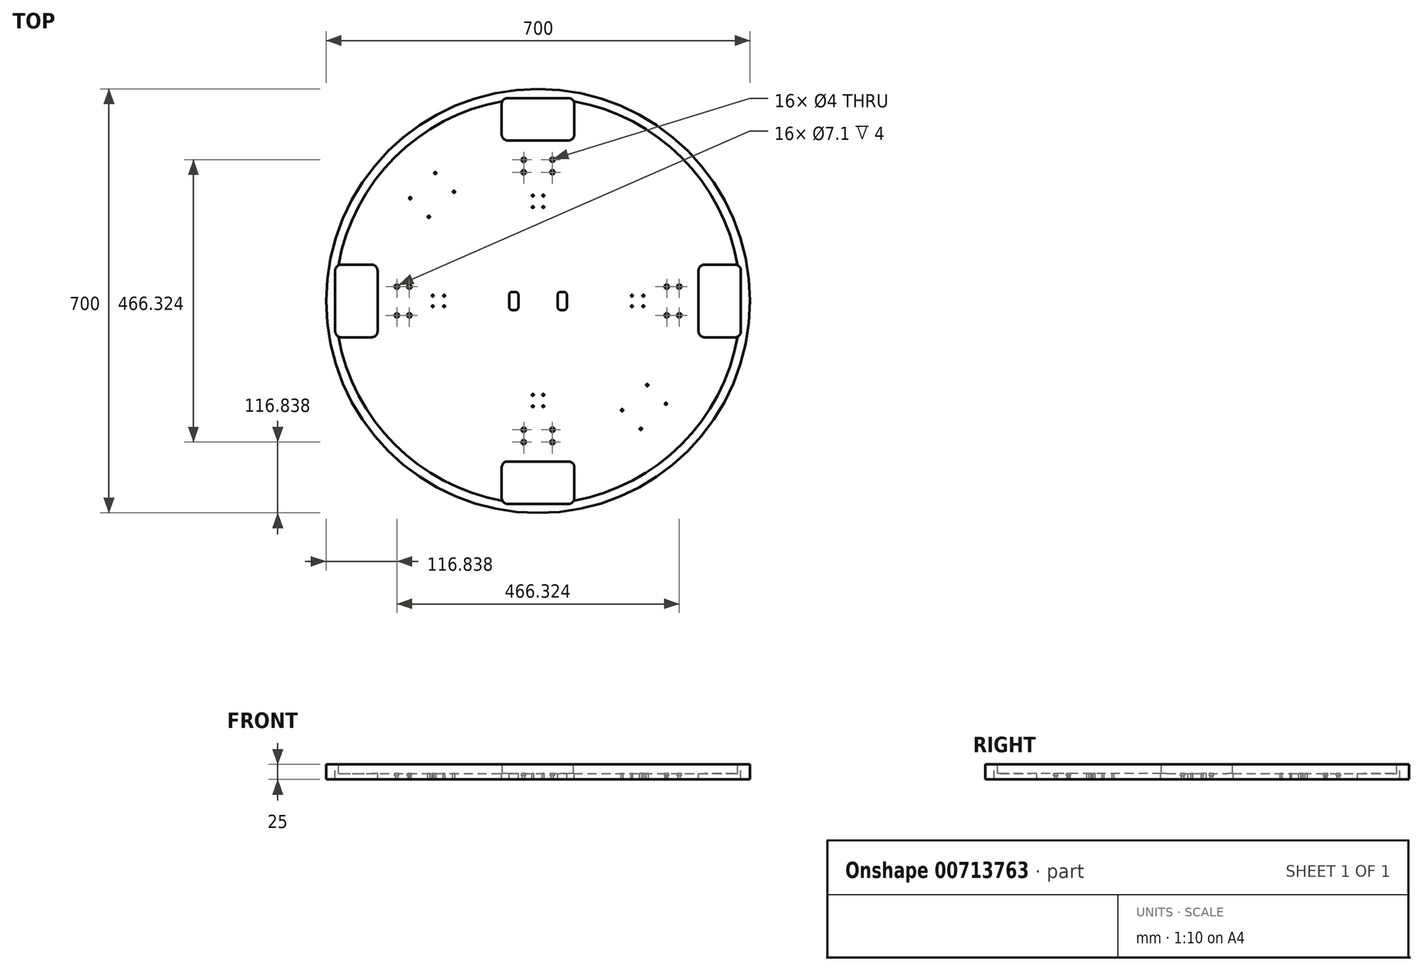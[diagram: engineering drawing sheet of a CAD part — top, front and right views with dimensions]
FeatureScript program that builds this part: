
annotation { "Feature Type Name" : "Feature", "Feature Type Description" : "" }
export const myFeature = defineFeature(function(context is Context, id is Id, definition is map)
    precondition{}
    {
        {
            var Q0;
            Q0=qCreatedBy(makeId("Top.planeOp"),FACE);
            var sketch = newSketch(context, id + "F0", { "sketchPlane" : qUnion([Q0])});
            skCircle(sketch, "E0", {"center": v(0, 0) * mm, "radius": 350 * mm});
            skSolve(sketch);
        }
        {
            var Q0;
            Q0 = qSketchRegion(id + "F0", true);
            extrude(context, id + "F1", {"entities" : qUnion([Q0]), "depth" : 25 * mm, "offsetDistance" : 25 * mm});
        }
        {
            var Q0;
            Q0=makeQuery(id+"F1.opExtrude","CAP_FACE",FACE,{"disambiguationData":[OSD([sQuery(id+"F0.wireOp",EDGE,"E0")])],"isStart":false});
            var sketch = newSketch(context, id + "F2", { "sketchPlane" : qUnion([Q0])});
            skLineSegment(sketch, "E1", {"start": v(0, 350) * mm, "end": v(0, -350) * mm});
            skLineSegment(sketch, "E2", {"start": v(-350, 0) * mm, "end": v(350, 0) * mm});
            skLineSegment(sketch, "E3.bottom", {"start": v(50, 265) * mm, "end": v(-50, 265) * mm});
            skLineSegment(sketch, "E3.top", {"start": v(50, 335) * mm, "end": v(-50, 335) * mm});
            skLineSegment(sketch, "E3.left", {"start": v(60, 275) * mm, "end": v(60, 325) * mm});
            skLineSegment(sketch, "E3.right", {"start": v(-60, 275) * mm, "end": v(-60, 325) * mm});
            skPoint(sketch, "E3.middle", {"position": v(0, 300) * mm});
            skPoint(sketch, "E4.visualSharp", {"position": v(-60, 335) * mm});
            skArc(sketch, "E4.filletArc", {"start": v(-50, 335) * mm, "mid": v(-57.07, 332.07) * mm, "end": v(-60, 325) * mm});
            skPoint(sketch, "E5.visualSharp", {"position": v(-60, 265) * mm});
            skArc(sketch, "E5.filletArc", {"start": v(-60, 275) * mm, "mid": v(-57.07, 267.93) * mm, "end": v(-50, 265) * mm});
            skPoint(sketch, "E6.visualSharp", {"position": v(60, 265) * mm});
            skArc(sketch, "E6.filletArc", {"start": v(50, 265) * mm, "mid": v(57.07, 267.93) * mm, "end": v(60, 275) * mm});
            skPoint(sketch, "E7.visualSharp", {"position": v(60, 335) * mm});
            skArc(sketch, "E7.filletArc", {"start": v(60, 325) * mm, "mid": v(57.07, 332.07) * mm, "end": v(50, 335) * mm});
            skLineSegment(sketch, "E8.bottom", {"start": v(-275, 60) * mm, "end": v(-325, 60) * mm});
            skLineSegment(sketch, "E8.top", {"start": v(-275, -60) * mm, "end": v(-325, -60) * mm});
            skLineSegment(sketch, "E8.left", {"start": v(-265, 50) * mm, "end": v(-265, -50) * mm});
            skLineSegment(sketch, "E8.right", {"start": v(-335, 50) * mm, "end": v(-335, -50) * mm});
            skPoint(sketch, "E8.middle", {"position": v(-300, 0) * mm});
            skPoint(sketch, "E9.visualSharp", {"position": v(-335, 60) * mm});
            skArc(sketch, "E9.filletArc", {"start": v(-325, 60) * mm, "mid": v(-332.07, 57.07) * mm, "end": v(-335, 50) * mm});
            skPoint(sketch, "E10.visualSharp", {"position": v(-265, 60) * mm});
            skArc(sketch, "E10.filletArc", {"start": v(-265, 50) * mm, "mid": v(-267.93, 57.07) * mm, "end": v(-275, 60) * mm});
            skPoint(sketch, "E11.visualSharp", {"position": v(-265, -60) * mm});
            skArc(sketch, "E11.filletArc", {"start": v(-275, -60) * mm, "mid": v(-267.93, -57.07) * mm, "end": v(-265, -50) * mm});
            skPoint(sketch, "E12.visualSharp", {"position": v(-335, -60) * mm});
            skArc(sketch, "E12.filletArc", {"start": v(-335, -50) * mm, "mid": v(-332.07, -57.07) * mm, "end": v(-325, -60) * mm});
            skLineSegment(sketch, "E13.bottom", {"start": v(50, -265) * mm, "end": v(-50, -265) * mm});
            skLineSegment(sketch, "E13.top", {"start": v(50, -335) * mm, "end": v(-50, -335) * mm});
            skLineSegment(sketch, "E13.left", {"start": v(60, -275) * mm, "end": v(60, -325) * mm});
            skLineSegment(sketch, "E13.right", {"start": v(-60, -275) * mm, "end": v(-60, -325) * mm});
            skPoint(sketch, "E13.middle", {"position": v(0, -300) * mm});
            skLineSegment(sketch, "E14.bottom", {"start": v(275, 60) * mm, "end": v(325, 60) * mm});
            skLineSegment(sketch, "E14.top", {"start": v(275, -60) * mm, "end": v(325, -60) * mm});
            skLineSegment(sketch, "E14.left", {"start": v(265, 50) * mm, "end": v(265, -50) * mm});
            skLineSegment(sketch, "E14.right", {"start": v(335, 50) * mm, "end": v(335, -50) * mm});
            skPoint(sketch, "E14.middle", {"position": v(300, 0) * mm});
            skPoint(sketch, "E15.visualSharp", {"position": v(265, 60) * mm});
            skArc(sketch, "E15.filletArc", {"start": v(275, 60) * mm, "mid": v(267.93, 57.07) * mm, "end": v(265, 50) * mm});
            skPoint(sketch, "E16.visualSharp", {"position": v(335, 60) * mm});
            skArc(sketch, "E16.filletArc", {"start": v(335, 50) * mm, "mid": v(332.07, 57.07) * mm, "end": v(325, 60) * mm});
            skPoint(sketch, "E17.visualSharp", {"position": v(335, -60) * mm});
            skArc(sketch, "E17.filletArc", {"start": v(325, -60) * mm, "mid": v(332.07, -57.07) * mm, "end": v(335, -50) * mm});
            skPoint(sketch, "E18.visualSharp", {"position": v(265, -60) * mm});
            skArc(sketch, "E18.filletArc", {"start": v(265, -50) * mm, "mid": v(267.93, -57.07) * mm, "end": v(275, -60) * mm});
            skPoint(sketch, "E19.visualSharp", {"position": v(60, -265) * mm});
            skArc(sketch, "E19.filletArc", {"start": v(60, -275) * mm, "mid": v(57.07, -267.93) * mm, "end": v(50, -265) * mm});
            skPoint(sketch, "E20.visualSharp", {"position": v(60, -335) * mm});
            skArc(sketch, "E20.filletArc", {"start": v(50, -335) * mm, "mid": v(57.07, -332.07) * mm, "end": v(60, -325) * mm});
            skPoint(sketch, "E21.visualSharp", {"position": v(-60, -335) * mm});
            skArc(sketch, "E21.filletArc", {"start": v(-60, -325) * mm, "mid": v(-57.07, -332.07) * mm, "end": v(-50, -335) * mm});
            skPoint(sketch, "E22.visualSharp", {"position": v(-60, -265) * mm});
            skArc(sketch, "E22.filletArc", {"start": v(-50, -265) * mm, "mid": v(-57.07, -267.93) * mm, "end": v(-60, -275) * mm});
            skSolve(sketch);
        }
        {
            var Q0;
            Q0 = qSketchRegion(id + "F2", true);
            extrude(context, id + "F3", {"entities" : qUnion([Q0]), "operationType" : NewBodyOperationType.REMOVE, "oppositeDirection" : true, "depth" : 25 * mm, "offsetDistance" : 25 * mm});
        }
        {
            var Q0;
            Q0=makeQuery(id+"F1.opExtrude","CAP_FACE",FACE,{"disambiguationData":[OSD([sQuery(id+"F0.wireOp",EDGE,"E0")])],"isStart":false});
            var sketch = newSketch(context, id + "F4", { "sketchPlane" : qUnion([Q0])});
            skCircle(sketch, "E23", {"center": v(0, 0) * mm, "radius": 335 * mm});
            skSolve(sketch);
        }
        {
            var Q0;
            Q0 = qSketchRegion(id + "F4", true);
            extrude(context, id + "F5", {"entities" : qUnion([Q0]), "operationType" : NewBodyOperationType.REMOVE, "oppositeDirection" : true, "depth" : 15 * mm, "offsetDistance" : 25 * mm});
        }
        {
            var Q0;
            Q0=makeQuery(id+"F5.boolean.opBoolean","COPY",FACE,{"derivedFrom":makeQuery(id+"F5.opExtrude","CAP_FACE",FACE,{"disambiguationData":[OSD([sQuery(id+"F4.wireOp",EDGE,"E23")])],"isStart":false})});
            var sketch = newSketch(context, id + "F6", { "sketchPlane" : qUnion([Q0])});
            skLineSegment(sketch, "E24", {"start": v(0, 0) * mm, "end": v(0, -360.17) * mm});
            skPoint(sketch, "E24.endSnap0", {"position": v(0, -265) * mm});
            skLineSegment(sketch, "E25", {"start": v(0, -360.17) * mm, "end": v(0, 359.9) * mm});
            skLineSegment(sketch, "E26", {"start": v(-341.98, 0) * mm, "end": v(360.15, 0) * mm});
            skPoint(sketch, "E27.middle", {"position": v(-222.85, 0) * mm});
            skCircle(sketch, "E28", {"center": v(-233.16, 23.69) * mm, "radius": 2 * mm});
            skCircle(sketch, "E29.MirrorC", {"center": v(-212.54, 23.69) * mm, "radius": 2 * mm});
            skCircle(sketch, "E30.MirrorC", {"center": v(-233.16, -23.69) * mm, "radius": 2 * mm});
            skCircle(sketch, "E31.MirrorC", {"center": v(-212.54, -23.69) * mm, "radius": 2 * mm});
            skPoint(sketch, "E32.orphan", {"position": v(-222.85, -27.5) * mm});
            skPoint(sketch, "E33.orphan", {"position": v(-207.85, 27.5) * mm});
            skPoint(sketch, "E34.orphan", {"position": v(-237.85, -27.5) * mm});
            skPoint(sketch, "E27.bottom.start.orphan", {"position": v(-207.85, -27.5) * mm});
            skPoint(sketch, "E27.top.end.orphan", {"position": v(-237.85, 27.5) * mm});
            skPoint(sketch, "E27.top.start.orphan", {"position": v(-222.85, 27.5) * mm});
            skCircle(sketch, "E35.1.0", {"center": v(-23.69, -233.16) * mm, "radius": 2 * mm});
            skCircle(sketch, "E35.1.1", {"center": v(-23.69, -212.54) * mm, "radius": 2 * mm});
            skCircle(sketch, "E35.1.2", {"center": v(23.69, -212.54) * mm, "radius": 2 * mm});
            skCircle(sketch, "E35.1.3", {"center": v(23.69, -233.16) * mm, "radius": 2 * mm});
            skCircle(sketch, "E35.2.0", {"center": v(233.16, -23.69) * mm, "radius": 2 * mm});
            skCircle(sketch, "E35.2.1", {"center": v(212.54, -23.69) * mm, "radius": 2 * mm});
            skCircle(sketch, "E35.2.2", {"center": v(212.54, 23.69) * mm, "radius": 2 * mm});
            skCircle(sketch, "E35.2.3", {"center": v(233.16, 23.69) * mm, "radius": 2 * mm});
            skCircle(sketch, "E35.3.0", {"center": v(23.69, 233.16) * mm, "radius": 2 * mm});
            skCircle(sketch, "E35.3.1", {"center": v(23.69, 212.54) * mm, "radius": 2 * mm});
            skCircle(sketch, "E35.3.2", {"center": v(-23.69, 212.54) * mm, "radius": 2 * mm});
            skCircle(sketch, "E35.3.3", {"center": v(-23.69, 233.16) * mm, "radius": 2 * mm});
            skPoint(sketch, "E35.center", {"position": v(0, 0) * mm});
            skLineSegment(sketch, "E36", {"start": v(-232.1, 23.69) * mm, "end": v(-231.16, 23.69) * mm});
            skLineSegment(sketch, "E37", {"start": v(-233.16, -23.69) * mm, "end": v(-231.16, -23.69) * mm});
            skCircle(sketch, "E38", {"center": v(-173.94, 8.69) * mm, "radius": 1.5 * mm});
            skCircle(sketch, "E39.MirrorC", {"center": v(-173.94, -8.69) * mm, "radius": 1.5 * mm});
            skCircle(sketch, "E40.MirrorC", {"center": v(-155, 8.69) * mm, "radius": 1.5 * mm});
            skLineSegment(sketch, "E41.trimOffspring", {"start": v(0, 23.69) * mm, "end": v(7.7, 23.69) * mm});
            skLineSegment(sketch, "E42.trimOffspring", {"start": v(-214.54, 23.69) * mm, "end": v(-210.54, 23.69) * mm});
            skLineSegment(sketch, "E43.trimOffspring", {"start": v(-214.54, -23.69) * mm, "end": v(-210.54, -23.69) * mm});
            skCircle(sketch, "E44.1.0", {"center": v(-8.69, -173.94) * mm, "radius": 1.5 * mm});
            skCircle(sketch, "E44.1.1", {"center": v(-8.69, -155) * mm, "radius": 1.5 * mm});
            skCircle(sketch, "E44.1.3", {"center": v(8.69, -173.94) * mm, "radius": 1.5 * mm});
            skCircle(sketch, "E44.2.0", {"center": v(173.94, -8.69) * mm, "radius": 1.5 * mm});
            skCircle(sketch, "E44.2.1", {"center": v(155, -8.69) * mm, "radius": 1.5 * mm});
            skCircle(sketch, "E44.2.3", {"center": v(173.94, 8.69) * mm, "radius": 1.5 * mm});
            skCircle(sketch, "E44.3.0", {"center": v(8.69, 173.94) * mm, "radius": 1.5 * mm});
            skCircle(sketch, "E44.3.1", {"center": v(8.69, 155) * mm, "radius": 1.5 * mm});
            skCircle(sketch, "E44.3.3", {"center": v(-8.69, 173.94) * mm, "radius": 1.5 * mm});
            skCircle(sketch, "E45.MirrorC", {"center": v(-155, -8.7) * mm, "radius": 1.5 * mm});
            skCircle(sketch, "E46.1.0", {"center": v(8.7, -155) * mm, "radius": 1.5 * mm});
            skCircle(sketch, "E46.2.0", {"center": v(155, 8.7) * mm, "radius": 1.5 * mm});
            skCircle(sketch, "E46.3.0", {"center": v(-8.7, 155) * mm, "radius": 1.5 * mm});
            skSolve(sketch);
        }
        {
            var Q0;
            Q0 = qSketchRegion(id + "F6", true);
            extrude(context, id + "F7", {"entities" : qUnion([Q0]), "operationType" : NewBodyOperationType.REMOVE, "oppositeDirection" : true, "depth" : 25 * mm, "offsetDistance" : 25 * mm});
        }
        {
            var Q0;
            Q0=makeQuery(id+"F5.boolean.opBoolean","COPY",FACE,{"derivedFrom":makeQuery(id+"F5.opExtrude","CAP_FACE",FACE,{"disambiguationData":[OSD([sQuery(id+"F4.wireOp",EDGE,"E23")])],"isStart":false})});
            var sketch = newSketch(context, id + "F8", { "sketchPlane" : qUnion([Q0])});
            skCircle(sketch, "E47", {"center": v(23.69, 233.16) * mm, "radius": 3.55 * mm});
            skCircle(sketch, "E48", {"center": v(23.69, 212.54) * mm, "radius": 3.55 * mm});
            skCircle(sketch, "E49", {"center": v(-23.69, 233.16) * mm, "radius": 3.55 * mm});
            skCircle(sketch, "E50", {"center": v(-23.69, 212.54) * mm, "radius": 3.55 * mm});
            skCircle(sketch, "E51.1.0", {"center": v(-212.54, 23.69) * mm, "radius": 3.55 * mm});
            skCircle(sketch, "E51.1.1", {"center": v(-233.16, 23.69) * mm, "radius": 3.55 * mm});
            skCircle(sketch, "E51.1.2", {"center": v(-233.16, -23.69) * mm, "radius": 3.55 * mm});
            skCircle(sketch, "E51.1.3", {"center": v(-212.54, -23.69) * mm, "radius": 3.55 * mm});
            skCircle(sketch, "E51.2.0", {"center": v(-23.69, -212.54) * mm, "radius": 3.55 * mm});
            skCircle(sketch, "E51.2.1", {"center": v(-23.69, -233.16) * mm, "radius": 3.55 * mm});
            skCircle(sketch, "E51.2.2", {"center": v(23.69, -233.16) * mm, "radius": 3.55 * mm});
            skCircle(sketch, "E51.2.3", {"center": v(23.69, -212.54) * mm, "radius": 3.55 * mm});
            skCircle(sketch, "E51.3.0", {"center": v(212.54, -23.69) * mm, "radius": 3.55 * mm});
            skCircle(sketch, "E51.3.1", {"center": v(233.16, -23.69) * mm, "radius": 3.55 * mm});
            skCircle(sketch, "E51.3.2", {"center": v(233.16, 23.69) * mm, "radius": 3.55 * mm});
            skCircle(sketch, "E51.3.3", {"center": v(212.54, 23.69) * mm, "radius": 3.55 * mm});
            skPoint(sketch, "E51.center", {"position": v(0, 0) * mm});
            skSolve(sketch);
        }
        {
            var Q0;
            Q0 = qSketchRegion(id + "F8", true);
            var Q1;
            Q1=makeQuery(id+"F1.opExtrude","CAP_FACE",FACE,{"disambiguationData":[OSD([sQuery(id+"F0.wireOp",EDGE,"E0")])],"isStart":true});
            extrude(context, id + "F9", {"entities" : qUnion([Q0]), "operationType" : NewBodyOperationType.REMOVE, "oppositeDirection" : true, "depth" : 4 * mm, "endBoundEntityFace" : qUnion([Q1]), "offsetDistance" : 25 * mm});
        }
        {
            var Q0;
            Q0=makeQuery(id+"F5.boolean.opBoolean","COPY",FACE,{"derivedFrom":makeQuery(id+"F5.opExtrude","CAP_FACE",FACE,{"disambiguationData":[OSD([sQuery(id+"F4.wireOp",EDGE,"E23")])],"isStart":false})});
            var sketch = newSketch(context, id + "F10", { "sketchPlane" : qUnion([Q0])});
            skLineSegment(sketch, "E52", {"start": v(-279.38, 0) * mm, "end": v(280, 0) * mm});
            skLineSegment(sketch, "E53.bottom", {"start": v(-42.5, -15) * mm, "end": v(-37.5, -15) * mm});
            skLineSegment(sketch, "E53.top", {"start": v(-42.5, 15) * mm, "end": v(-37.5, 15) * mm});
            skLineSegment(sketch, "E53.left", {"start": v(-47.5, -10) * mm, "end": v(-47.5, 10) * mm});
            skLineSegment(sketch, "E53.right", {"start": v(-32.5, -10) * mm, "end": v(-32.5, 10) * mm});
            skPoint(sketch, "E53.middle", {"position": v(-40, 0) * mm});
            skPoint(sketch, "E54.visualSharp", {"position": v(-32.5, -15) * mm});
            skArc(sketch, "E54.filletArc", {"start": v(-37.5, -15) * mm, "mid": v(-33.96, -13.54) * mm, "end": v(-32.5, -10) * mm});
            skPoint(sketch, "E55.visualSharp", {"position": v(-47.5, -15) * mm});
            skArc(sketch, "E55.filletArc", {"start": v(-47.5, -10) * mm, "mid": v(-46.04, -13.54) * mm, "end": v(-42.5, -15) * mm});
            skPoint(sketch, "E56.visualSharp", {"position": v(-32.5, 15) * mm});
            skArc(sketch, "E56.filletArc", {"start": v(-32.5, 10) * mm, "mid": v(-33.96, 13.54) * mm, "end": v(-37.5, 15) * mm});
            skPoint(sketch, "E57.visualSharp", {"position": v(-47.5, 15) * mm});
            skArc(sketch, "E57.filletArc", {"start": v(-42.5, 15) * mm, "mid": v(-46.04, 13.54) * mm, "end": v(-47.5, 10) * mm});
            skLineSegment(sketch, "E58.1.0", {"start": v(47.5, 10) * mm, "end": v(47.5, -10) * mm});
            skLineSegment(sketch, "E58.1.1", {"start": v(32.5, 10) * mm, "end": v(32.5, -10) * mm});
            skLineSegment(sketch, "E58.1.2", {"start": v(42.5, -15) * mm, "end": v(37.5, -15) * mm});
            skLineSegment(sketch, "E58.1.3", {"start": v(42.5, 15) * mm, "end": v(37.5, 15) * mm});
            skArc(sketch, "E58.1.4", {"start": v(37.5, 15) * mm, "mid": v(33.96, 13.54) * mm, "end": v(32.5, 10) * mm});
            skArc(sketch, "E58.1.5", {"start": v(47.5, 10) * mm, "mid": v(46.04, 13.54) * mm, "end": v(42.5, 15) * mm});
            skPoint(sketch, "E58.1.6", {"position": v(32.5, 15) * mm});
            skPoint(sketch, "E58.1.7", {"position": v(47.5, 15) * mm});
            skPoint(sketch, "E58.1.8", {"position": v(40, 0) * mm});
            skArc(sketch, "E58.1.9", {"start": v(32.5, -10) * mm, "mid": v(33.96, -13.54) * mm, "end": v(37.5, -15) * mm});
            skPoint(sketch, "E58.1.10", {"position": v(32.5, -15) * mm});
            skArc(sketch, "E58.1.11", {"start": v(42.5, -15) * mm, "mid": v(46.04, -13.54) * mm, "end": v(47.5, -10) * mm});
            skPoint(sketch, "E58.1.12", {"position": v(47.5, -15) * mm});
            skPoint(sketch, "E58.center", {"position": v(0, 0) * mm});
            skSolve(sketch);
        }
        {
            var Q0;
            Q0 = qSketchRegion(id + "F10", true);
            extrude(context, id + "F11", {"entities" : qUnion([Q0]), "operationType" : NewBodyOperationType.REMOVE, "oppositeDirection" : true, "depth" : 25 * mm, "offsetDistance" : 25 * mm});
        }
        {
            var Q0;
            Q0=makeQuery(id+"F5.boolean.opBoolean","COPY",FACE,{"derivedFrom":makeQuery(id+"F5.opExtrude","CAP_FACE",FACE,{"disambiguationData":[OSD([sQuery(id+"F4.wireOp",EDGE,"E23")])],"isStart":false})});
            var sketch = newSketch(context, id + "F12", { "sketchPlane" : qUnion([Q0])});
            skLineSegment(sketch, "E59", {"start": v(-236.88, 236.88) * mm, "end": v(236.88, -236.88) * mm});
            skCircle(sketch, "E60", {"center": v(-169.7, 211.19) * mm, "radius": 1.78 * mm});
            skCircle(sketch, "E61.MirrorC", {"center": v(-211.19, 169.7) * mm, "radius": 1.78 * mm});
            skCircle(sketch, "E62.MirrorC", {"center": v(-180.32, 138.83) * mm, "radius": 1.78 * mm});
            skCircle(sketch, "E63.MirrorC", {"center": v(-138.83, 180.32) * mm, "radius": 1.78 * mm});
            skPoint(sketch, "E64.orphan", {"position": v(-169.7, 123) * mm});
            skPoint(sketch, "E65.orphan", {"position": v(-198.36, 151.66) * mm});
            skPoint(sketch, "E66.orphan", {"position": v(-180.57, 133.87) * mm});
            skPoint(sketch, "E67.orphan", {"position": v(-133.87, 180.57) * mm});
            skPoint(sketch, "E68.start.orphan", {"position": v(-227.02, 180.32) * mm});
            skCircle(sketch, "E69.1.0", {"center": v(211.19, -169.7) * mm, "radius": 1.78 * mm});
            skCircle(sketch, "E69.1.1", {"center": v(180.32, -138.83) * mm, "radius": 1.78 * mm});
            skCircle(sketch, "E69.1.2", {"center": v(138.83, -180.32) * mm, "radius": 1.78 * mm});
            skCircle(sketch, "E69.1.3", {"center": v(169.7, -211.19) * mm, "radius": 1.78 * mm});
            skPoint(sketch, "E69.center", {"position": v(0, 0) * mm});
            skSolve(sketch);
        }
        {
            var Q0;
            Q0 = qSketchRegion(id + "F12", true);
            extrude(context, id + "F13", {"entities" : qUnion([Q0]), "operationType" : NewBodyOperationType.REMOVE, "oppositeDirection" : true, "depth" : 25 * mm, "offsetDistance" : 25 * mm});
        }
    });
